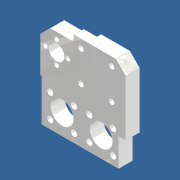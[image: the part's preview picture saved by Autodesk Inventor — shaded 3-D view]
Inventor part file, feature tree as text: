
AUTODESK INVENTOR PART (.ipt)
format: ipt  version: 2020 (Build 240168000, 168)  size: 326,656 bytes
history: native  units: mm
features: sketch x7, extrude x6, hole x1, direct_edit x1, chamfer x1, fillet x1, move_body x1
ambient origin geometry x8: Origin, YZ Plane, XZ Plane, XY Plane, X Axis, Y Axis, Z Axis, Center Point
bodies: Solid1 (feature_tree)
feature tree (18):
  extrude  "Extrusion1"  Depth=67.0mm
  hole  "Hole1"  [1 undecoded]
  extrude  "Extrusion4"  Depth=22.0mm
  extrude  "Extrusion5"  Depth=10.0mm TaperAngle=0.0deg
  extrude  "Extrusion6"  Depth=10.0mm
  extrude  "Extrusion7"  Depth=3.5mm
  extrude  "Extrusion8"  Depth=2.0mm TaperAngle=360.0deg
  direct_edit  "Direct Edit1"
  chamfer  "Chamfer2"  [1 undecoded]
  fillet  "Fillet1"  Radius=17.0mm
  sketch  "Sketch1"  dims[d0=65.0mm d1=67.0mm]
  sketch  "Sketch5"  dims[d2=10.0mm d3=0.0mm d30=6.0mm]
  sketch  "Sketch6"  dims[d31=4.0mm d32=22.0mm]
  sketch  "Sketch7"  dims[d33=4.0mm d34=6.0mm d35=9.0mm d36=3.0mm d37=90.0deg d38=8.0mm d39=20.594885mm d40=10.0mm d41=0.0mm]
  sketch  "Sketch8"  dims[d50=22.0mm d51=10.0mm]
  sketch  "Sketch9"  dims[d52=11.5mm d54=3.5mm]
  sketch  "Sketch10"  dims[d55=16.0mm d59=40.0mm d61=360.0deg d63=0.0mm d64=0.0mm d65=17.0mm d66=49.5mm d67=5.0mm d68=5.0mm d69=30.0mm d70=0.0mm d71=0.0mm d72=20.0mm d73=4.0mm d74=3.0mm d75=0.0mm d76=0.0mm d77=2.0mm d78=4.5mm d79=16.5mm d80=16.5mm d81=4.5mm d82=4.5mm d83=4.5mm d84=4.5mm d85=4.5mm d86=4.5mm d87=4.5mm d88=4.5mm d89=0.0mm d90=0.0mm d91=0.0mm d92=0.0mm d93=-4.0mm d94=7.0mm d95=2.0mm d96=45.0deg d97=2.0mm]
  move_body  "Move1"
note: 2 required parameter values undecoded (feature->parameter linkage not recoverable at this tier; creation-order binding heuristic only, values carry confidence <= 0.55)
